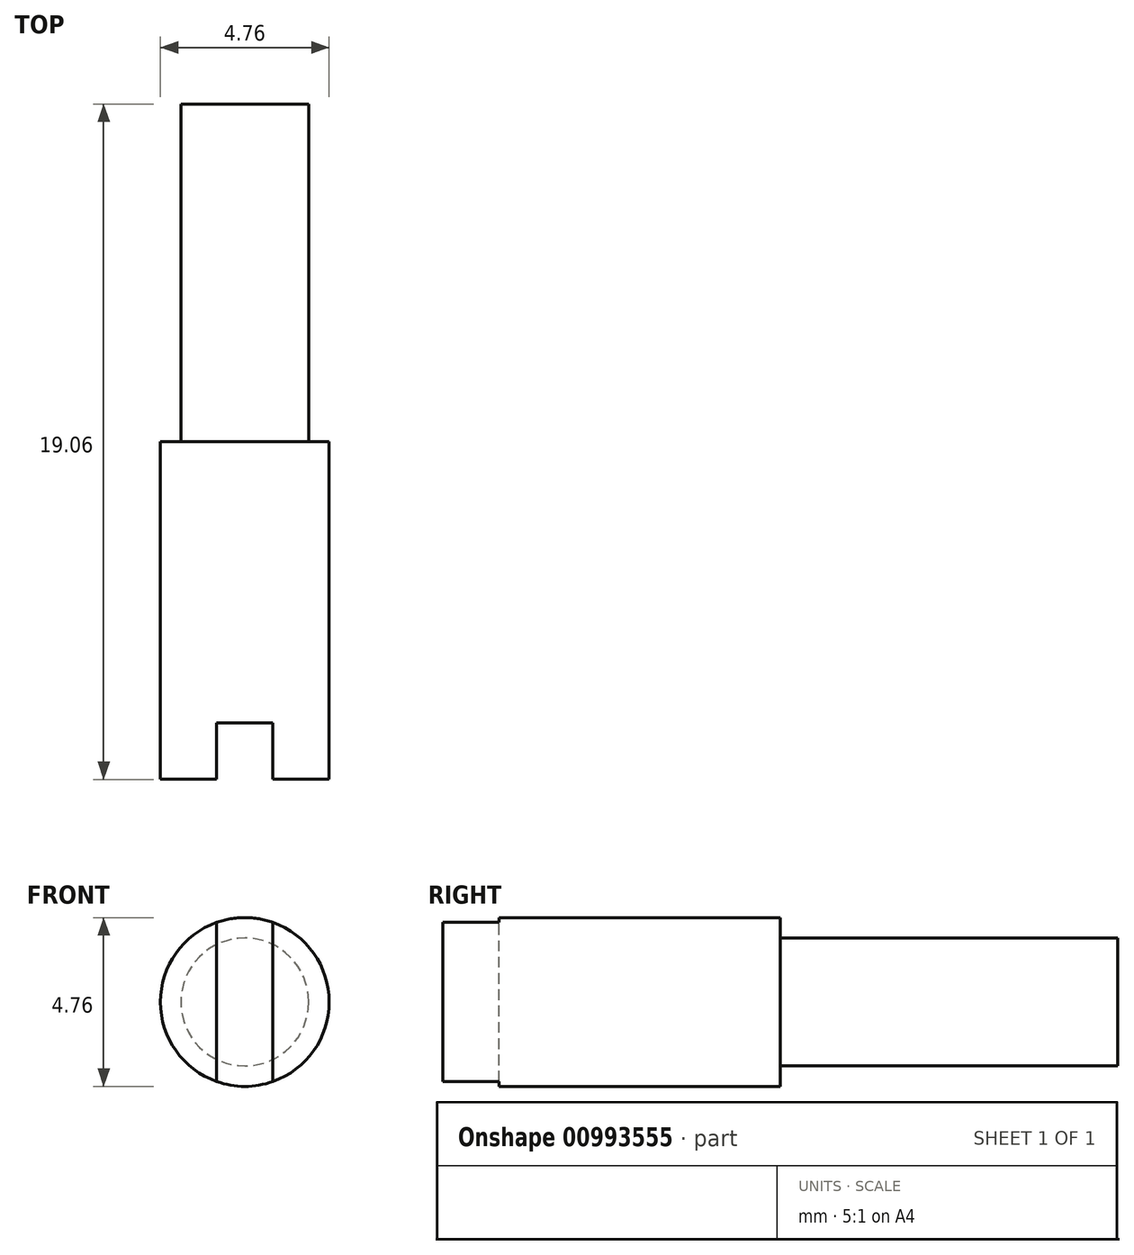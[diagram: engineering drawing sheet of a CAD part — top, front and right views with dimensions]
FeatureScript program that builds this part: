
annotation { "Feature Type Name" : "Feature", "Feature Type Description" : "" }
export const myFeature = defineFeature(function(context is Context, id is Id, definition is map)
    precondition{}
    {
        {
            var Q0;
            Q0=qCreatedBy(makeId("Front.planeOp"),FACE);
            var sketch = newSketch(context, id + "F0", { "sketchPlane" : qUnion([Q0])});
            skLineSegment(sketch, "E0.bottom", {"start": v(-2.38, -2.38) * mm, "end": v(2.38, -2.38) * mm});
            skLineSegment(sketch, "E0.top", {"start": v(-2.38, 2.38) * mm, "end": v(2.38, 2.38) * mm});
            skLineSegment(sketch, "E0.left", {"start": v(-2.38, -2.38) * mm, "end": v(-2.38, 2.38) * mm});
            skLineSegment(sketch, "E0.right", {"start": v(2.38, -2.38) * mm, "end": v(2.38, 2.38) * mm});
            skPoint(sketch, "E0.middle", {"position": v(0, 0) * mm});
            skSolve(sketch);
        }
        {
            var Q0;
            Q0=makeQuery(id+"F0.imprint","IMPRINT",FACE,{"disambiguationData":[TD([[makeQuery(id+"F0.imprint","IMPRINT",EDGE,{"derivedFrom":sQuery(id+"F0.wireOp",EDGE,"E0.bottom")}),1.0]])]});
            extrude(context, id + "F1", {"entities" : qUnion([Q0]), "depth" : 9.52 * mm, "offsetDistance" : 25.4 * mm});
        }
        {
            var Q0;
            Q0=makeQuery(id+"F1.opExtrude","SWEPT_FACE",FACE,{"disambiguationData":[OSD([sQuery(id+"F0.wireOp",EDGE,"E0.top")])]});
            var sketch = newSketch(context, id + "F2", { "sketchPlane" : qUnion([Q0])});
            skLineSegment(sketch, "E1", {"start": v(0, -9.53) * mm, "end": v(-0.8, -9.53) * mm});
            skLineSegment(sketch, "E2", {"start": v(-0.8, -9.53) * mm, "end": v(0.8, -9.53) * mm});
            skLineSegment(sketch, "E3", {"start": v(0.8, -9.53) * mm, "end": v(0.8, -7.94) * mm});
            skLineSegment(sketch, "E4", {"start": v(-0.8, -9.53) * mm, "end": v(-0.8, -7.94) * mm});
            skLineSegment(sketch, "E5", {"start": v(-0.8, -7.94) * mm, "end": v(0.8, -7.94) * mm});
            skSolve(sketch);
        }
        {
            var Q0;
            {var subQ3=sQuery(id+"F2.wireOp",EDGE,"E3");Q0=makeQuery(id+"F2.imprint","IMPRINT",FACE,{"disambiguationData":[TD([[makeQuery(id+"F2.imprint","IMPRINT",EDGE,{"derivedFrom":subQ3}),1.0]])]});}
            extrude(context, id + "F3", {"entities" : qUnion([Q0]), "operationType" : NewBodyOperationType.REMOVE, "oppositeDirection" : true, "depth" : 25.4 * mm, "offsetDistance" : 25.4 * mm});
        }
        {
            var Q0;
            Q0=makeQuery(id+"F1.opExtrude","CAP_FACE",FACE,{"disambiguationData":[OSD([sQuery(id+"F0.wireOp",EDGE,"E0.bottom"),sQuery(id+"F0.wireOp",EDGE,"E0.top"),sQuery(id+"F0.wireOp",EDGE,"E0.left"),sQuery(id+"F0.wireOp",EDGE,"E0.right")])],"isStart":true});
            var sketch = newSketch(context, id + "F4", { "sketchPlane" : qUnion([Q0])});
            skCircle(sketch, "E6", {"center": v(0, 0) * mm, "radius": 2.38 * mm});
            skSolve(sketch);
        }
        {
            var Q0;
            {var subQ0=sQuery(id+"F4.wireOp",EDGE,"E6");var subQ1=makeQuery(id+"F1.opExtrude","CAP_EDGE",EDGE,{"disambiguationData":[OSD([sQuery(id+"F0.wireOp",EDGE,"E0.top")])],"isStart":true});var subQ2=makeQuery(id+"F4.imprint","INTERSECT",VERTEX,{"derivedFrom":[subQ1,subQ0]});Q0=makeQuery(id+"F4.imprint","IMPRINT",FACE,{"disambiguationData":[TD([[makeQuery(id+"F4.imprint","IMPRINT",EDGE,{"disambiguationData":[TD([[subQ2,-1.0]])],"derivedFrom":subQ0}),-1.0]])]});}
            var Q1;
            {var subQ0=sQuery(id+"F4.wireOp",EDGE,"E6");var subQ1=makeQuery(id+"F1.opExtrude","CAP_EDGE",EDGE,{"disambiguationData":[OSD([sQuery(id+"F0.wireOp",EDGE,"E0.top")])],"isStart":true});var subQ2=makeQuery(id+"F4.imprint","INTERSECT",VERTEX,{"derivedFrom":[subQ1,subQ0]});Q1=makeQuery(id+"F4.imprint","IMPRINT",FACE,{"disambiguationData":[TD([[makeQuery(id+"F4.imprint","IMPRINT",EDGE,{"disambiguationData":[TD([[subQ2,1.0]])],"derivedFrom":subQ0}),-1.0]])]});}
            var Q2;
            {var subQ0=sQuery(id+"F4.wireOp",EDGE,"E6");var subQ1=makeQuery(id+"F1.opExtrude","CAP_EDGE",EDGE,{"disambiguationData":[OSD([sQuery(id+"F0.wireOp",EDGE,"E0.left")])],"isStart":true});var subQ2=makeQuery(id+"F4.imprint","INTERSECT",VERTEX,{"derivedFrom":[subQ1,subQ0]});Q2=makeQuery(id+"F4.imprint","IMPRINT",FACE,{"disambiguationData":[TD([[makeQuery(id+"F4.imprint","IMPRINT",EDGE,{"disambiguationData":[TD([[subQ2,1.0]])],"derivedFrom":subQ0}),-1.0]])]});}
            var Q3;
            {var subQ0=sQuery(id+"F4.wireOp",EDGE,"E6");var subQ1=makeQuery(id+"F1.opExtrude","CAP_EDGE",EDGE,{"disambiguationData":[OSD([sQuery(id+"F0.wireOp",EDGE,"E0.right")])],"isStart":true});var subQ2=makeQuery(id+"F4.imprint","INTERSECT",VERTEX,{"derivedFrom":[subQ1,subQ0]});Q3=makeQuery(id+"F4.imprint","IMPRINT",FACE,{"disambiguationData":[TD([[makeQuery(id+"F4.imprint","IMPRINT",EDGE,{"disambiguationData":[TD([[subQ2,-1.0]])],"derivedFrom":subQ0}),-1.0]])]});}
            extrude(context, id + "F5", {"entities" : qUnion([Q0, Q1, Q2, Q3]), "operationType" : NewBodyOperationType.REMOVE, "oppositeDirection" : true, "depth" : 25.4 * mm, "offsetDistance" : 25.4 * mm});
        }
        {
            var Q0;
            Q0=makeQuery(id+"F1.opExtrude","CAP_FACE",FACE,{"disambiguationData":[OSD([sQuery(id+"F0.wireOp",EDGE,"E0.bottom"),sQuery(id+"F0.wireOp",EDGE,"E0.top"),sQuery(id+"F0.wireOp",EDGE,"E0.left"),sQuery(id+"F0.wireOp",EDGE,"E0.right")])],"isStart":true});
            var sketch = newSketch(context, id + "F6", { "sketchPlane" : qUnion([Q0])});
            skCircle(sketch, "E7", {"center": v(0, 0) * mm, "radius": 1.8 * mm});
            skSolve(sketch);
        }
        {
            var Q0;
            Q0=makeQuery(id+"F6.imprint","IMPRINT",FACE,{"disambiguationData":[TD([[makeQuery(id+"F6.imprint","IMPRINT",EDGE,{"derivedFrom":sQuery(id+"F6.wireOp",EDGE,"E7")}),1.0]])]});
            extrude(context, id + "F7", {"entities" : qUnion([Q0]), "operationType" : NewBodyOperationType.ADD, "depth" : 9.52 * mm, "offsetDistance" : 25.4 * mm});
        }
    });
